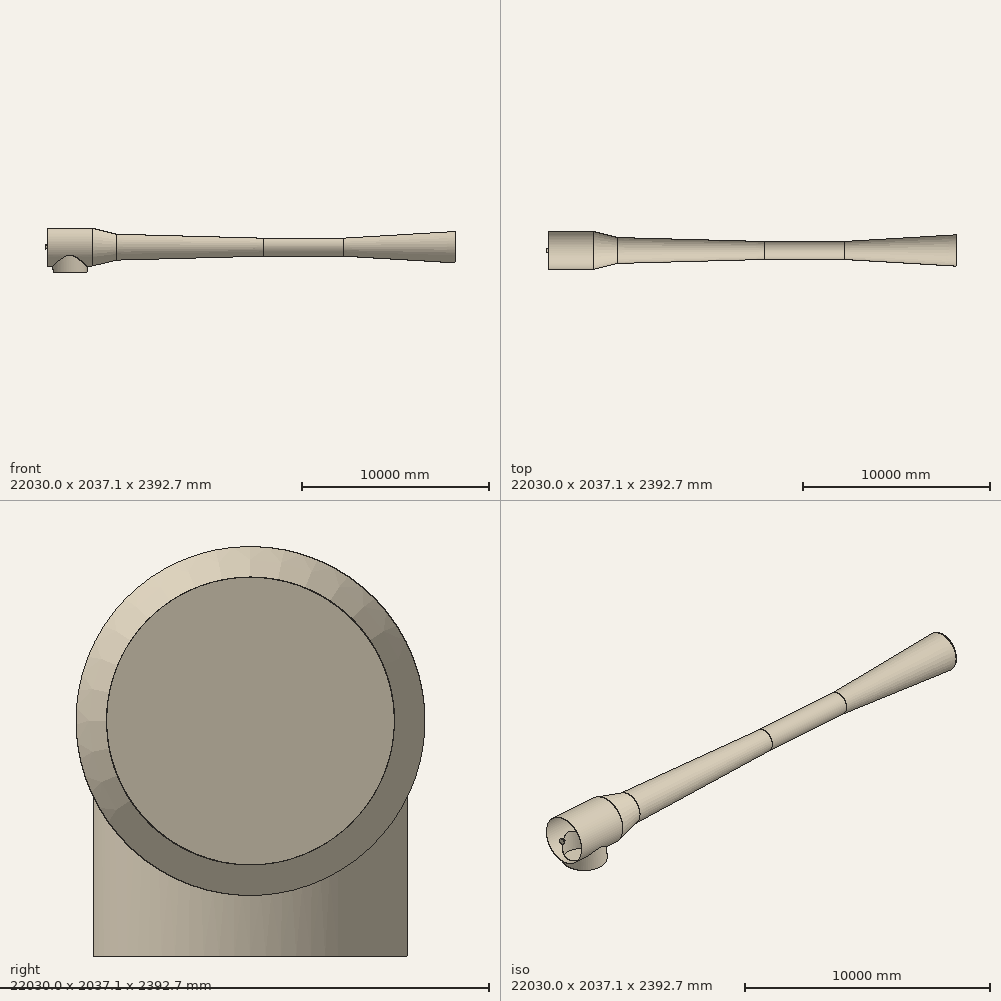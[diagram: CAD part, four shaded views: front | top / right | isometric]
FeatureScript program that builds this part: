
annotation { "Feature Type Name" : "Feature", "Feature Type Description" : "" }
export const myFeature = defineFeature(function(context is Context, id is Id, definition is map)
    precondition{}
    {
        {
            var Q0;
            Q0=qCreatedBy(makeId("Right.planeOp"),FACE);
            var sketch = newSketch(context, id + "F0", { "sketchPlane" : qUnion([Q0])});
            skCircle(sketch, "E0", {"center": v(0, 0) * mm, "radius": 1017.27 * mm});
            skSolve(sketch);
        }
        {
            var Q0;
            Q0 = qSketchRegion(id + "F0", true);
            extrude(context, id + "F1", {"entities" : qUnion([Q0]), "oppositeDirection" : true, "depth" : 2389.63 * mm});
        }
        {
            var Q0;
            Q0=makeQuery(id+"F1.opExtrude","CAP_FACE",FACE,{"disambiguationData":[OSD([sQuery(id+"F0.wireOp",EDGE,"E0")])],"isStart":true});
            shell(context, id + "F2", {"entities" : qUnion([Q0]), "thickness" : 2.54 * mm});
        }
        {
            var Q0;
            Q0=qCreatedBy(makeId("Top.planeOp"),FACE);
            var sketch = newSketch(context, id + "F3", { "sketchPlane" : qUnion([Q0])});
            skLineSegment(sketch, "E1", {"start": v(0, 0) * mm, "end": v(-2389.63, 0) * mm, "construction": true});
            skLineSegment(sketch, "E2", {"start": v(0, 0) * mm, "end": v(-1194.82, 0) * mm, "construction": true});
            skCircle(sketch, "E3", {"center": v(-1194.82, 0) * mm, "radius": 914.4 * mm});
            skCircle(sketch, "E4", {"center": v(-1194.82, 0) * mm, "radius": 915.67 * mm});
            skSolve(sketch);
        }
        {
            var Q0;
            Q0 = qSketchRegion(id + "F3", true);
            extrude(context, id + "F4", {"entities" : qUnion([Q0]), "oppositeDirection" : true, "depth" : 1371.6 * mm});
        }
        {
            var Q0;
            Q0=qCreatedBy(makeId("Right.planeOp"),FACE);
            var sketch = newSketch(context, id + "F5", { "sketchPlane" : qUnion([Q0])});
            skCircle(sketch, "E5", {"center": v(0, 0) * mm, "radius": 33.13 * mm});
            skSolve(sketch);
        }
        {
            var Q0;
            Q0 = qSketchRegion(id + "F5", true);
            extrude(context, id + "F6", {"entities" : qUnion([Q0]), "operationType" : NewBodyOperationType.REMOVE, "oppositeDirection" : true, "depth" : 2389.63 * mm});
        }
        {
            var Q0;
            Q0=qCreatedBy(makeId("Top.planeOp"),FACE);
            var sketch = newSketch(context, id + "F7", { "sketchPlane" : qUnion([Q0])});
            skLineSegment(sketch, "E6", {"start": v(0, 0) * mm, "end": v(-1194.82, 0) * mm});
            skCircle(sketch, "E7", {"center": v(-1194.82, 0) * mm, "radius": 914.4 * mm});
            skSolve(sketch);
        }
        {
            var Q0;
            Q0 = qSketchRegion(id + "F7", true);
            extrude(context, id + "F8", {"entities" : qUnion([Q0]), "operationType" : NewBodyOperationType.REMOVE, "oppositeDirection" : true, "depth" : 1018.54 * mm});
        }
        {
            var Q0;
            Q0=qCreatedBy(makeId("Front.planeOp"),FACE);
            var sketch = newSketch(context, id + "F9", { "sketchPlane" : qUnion([Q0])});
            skLineSegment(sketch, "E8", {"start": v(0, 0) * mm, "end": v(-2389.63, 0) * mm, "construction": true});
            skLineSegment(sketch, "E9", {"start": v(-2389.63, 33.13) * mm, "end": v(-2389.63, -33.13) * mm, "construction": true});
            skLineSegment(sketch, "E10", {"start": v(-2389.63, 33.13) * mm, "end": v(-1410.29, 241.3) * mm});
            skLineSegment(sketch, "E11", {"start": v(-2389.63, 33.13) * mm, "end": v(-2487.4, 101.59) * mm});
            skLineSegment(sketch, "E12", {"start": v(-2389.63, 33.13) * mm, "end": v(-1410.29, 33.13) * mm, "construction": true});
            skLineSegment(sketch, "E13", {"start": v(-2389.63, 58.53) * mm, "end": v(-2389.63, -58.53) * mm, "construction": true});
            skLineSegment(sketch, "E14", {"start": v(-2389.63, 58.53) * mm, "end": v(-1410.29, 266.7) * mm});
            skLineSegment(sketch, "E15", {"start": v(-2389.63, 58.53) * mm, "end": v(-2487.4, 126.99) * mm});
            skLineSegment(sketch, "E16", {"start": v(-2389.63, -33.13) * mm, "end": v(-2389.63, -58.53) * mm});
            skLineSegment(sketch, "E17", {"start": v(-2389.63, 33.13) * mm, "end": v(-2389.63, 58.53) * mm});
            skLineSegment(sketch, "E18", {"start": v(-1410.29, 266.7) * mm, "end": v(-1410.29, 241.3) * mm});
            skLineSegment(sketch, "E19", {"start": v(-2487.41, 33.13) * mm, "end": v(-2389.63, 33.13) * mm, "construction": true});
            skLineSegment(sketch, "E20", {"start": v(-2487.4, 101.59) * mm, "end": v(-2487.4, 126.99) * mm});
            skSolve(sketch);
        }
        {
            var Q0;
            Q0 = qSketchRegion(id + "F9", true);
            var Q1;
            Q1=sQuery(id+"F9.wireOp",EDGE,"E8");
            revolve(context, id + "F10", {"entities" : qUnion([Q0]), "axis" : qUnion([Q1]), "revolveType" : RevolveType.FULL});
        }
        {
            var Q0;
            Q0=makeQuery(id+"F10.opRevolve","SWEPT_FACE",FACE,{"disambiguationData":[OSD([sQuery(id+"F9.wireOp",EDGE,"E18")])]});
            var sketch = newSketch(context, id + "F11", { "sketchPlane" : qUnion([Q0])});
            skCircle(sketch, "E21", {"center": v(0, 0) * mm, "radius": 266.7 * mm});
            skSolve(sketch);
        }
        {
            var Q0;
            Q0 = qSketchRegion(id + "F11", true);
            extrude(context, id + "F12", {"entities" : qUnion([Q0]), "operationType" : NewBodyOperationType.ADD, "depth" : 2.54 * mm});
        }
        {
            var Q0;
            Q0=qCreatedBy(makeId("Front.planeOp"),FACE);
            var sketch = newSketch(context, id + "F13", { "sketchPlane" : qUnion([Q0])});
            skLineSegment(sketch, "E22", {"start": v(0, 0) * mm, "end": v(1319.48, 0) * mm, "construction": true});
            skLineSegment(sketch, "E23", {"start": v(0, 0) * mm, "end": v(0, 1016) * mm, "construction": true});
            skLineSegment(sketch, "E24", {"start": v(1319.48, 0) * mm, "end": v(1319.48, 693.42) * mm, "construction": true});
            skLineSegment(sketch, "E25", {"start": v(0, 1016) * mm, "end": v(1319.48, 693.42) * mm});
            skLineSegment(sketch, "E26", {"start": v(0, 1018.54) * mm, "end": v(1319.48, 695.96) * mm});
            skLineSegment(sketch, "E27", {"start": v(0, 1016) * mm, "end": v(0, 1018.54) * mm});
            skLineSegment(sketch, "E28", {"start": v(1319.48, 695.96) * mm, "end": v(1319.48, 693.42) * mm});
            skSolve(sketch);
        }
        {
            var Q0;
            Q0 = qSketchRegion(id + "F13", true);
            var Q1;
            Q1=sQuery(id+"F13.wireOp",EDGE,"E22");
            revolve(context, id + "F14", {"operationType" : NewBodyOperationType.ADD, "entities" : qUnion([Q0]), "axis" : qUnion([Q1]), "revolveType" : RevolveType.FULL});
        }
        {
            var Q0;
            Q0=qCreatedBy(makeId("Front.planeOp"),FACE);
            var sketch = newSketch(context, id + "F15", { "sketchPlane" : qUnion([Q0])});
            skLineSegment(sketch, "E29", {"start": v(0, 0) * mm, "end": v(1319.48, 0) * mm, "construction": true});
            skLineSegment(sketch, "E30", {"start": v(1319.48, 0) * mm, "end": v(1319.48, 693.42) * mm, "construction": true});
            skLineSegment(sketch, "E31", {"start": v(1319.48, 0) * mm, "end": v(9201.6, 0) * mm, "construction": true});
            skLineSegment(sketch, "E32", {"start": v(9201.6, 0) * mm, "end": v(9201.6, 481.01) * mm, "construction": true});
            skLineSegment(sketch, "E33", {"start": v(1319.48, 693.42) * mm, "end": v(9201.6, 481.01) * mm});
            skLineSegment(sketch, "E34", {"start": v(1319.48, 695.96) * mm, "end": v(9201.6, 483.55) * mm});
            skLineSegment(sketch, "E35", {"start": v(9201.6, 481.01) * mm, "end": v(9201.6, 483.55) * mm});
            skLineSegment(sketch, "E36", {"start": v(1319.48, 695.96) * mm, "end": v(1319.48, 693.42) * mm});
            skSolve(sketch);
        }
        {
            var Q0;
            Q0 = qSketchRegion(id + "F15", true);
            var Q1;
            Q1=sQuery(id+"F15.wireOp",EDGE,"E31");
            revolve(context, id + "F16", {"operationType" : NewBodyOperationType.ADD, "entities" : qUnion([Q0]), "axis" : qUnion([Q1]), "revolveType" : RevolveType.FULL});
        }
        {
            var Q0;
            Q0=makeQuery(id+"F16.opRevolve","SWEPT_FACE",FACE,{"disambiguationData":[OSD([sQuery(id+"F15.wireOp",EDGE,"E35")])]});
            var sketch = newSketch(context, id + "F17", { "sketchPlane" : qUnion([Q0])});
            skCircle(sketch, "E37", {"center": v(0, 0) * mm, "radius": 481.01 * mm});
            skCircle(sketch, "E38", {"center": v(0, 0) * mm, "radius": 482.28 * mm});
            skSolve(sketch);
        }
        {
            var Q0;
            Q0 = qSketchRegion(id + "F17", true);
            extrude(context, id + "F18", {"entities" : qUnion([Q0]), "operationType" : NewBodyOperationType.ADD, "depth" : 4302.12 * mm});
        }
        {
            var Q0;
            Q0=qCreatedBy(makeId("Front.planeOp"),FACE);
            var sketch = newSketch(context, id + "F19", { "sketchPlane" : qUnion([Q0])});
            skLineSegment(sketch, "E39", {"start": v(0, 0) * mm, "end": v(13503.73, 0) * mm, "construction": true});
            skLineSegment(sketch, "E40", {"start": v(13503.73, 0) * mm, "end": v(13503.73, 481.01) * mm, "construction": true});
            skLineSegment(sketch, "E41", {"start": v(13503.73, 0) * mm, "end": v(19491.78, 0) * mm, "construction": true});
            skLineSegment(sketch, "E42", {"start": v(19491.78, 0) * mm, "end": v(19491.78, 838.2) * mm, "construction": true});
            skLineSegment(sketch, "E43", {"start": v(13503.73, 481.01) * mm, "end": v(19491.78, 838.2) * mm});
            skLineSegment(sketch, "E44", {"start": v(13503.73, 481.01) * mm, "end": v(13503.73, 483.55) * mm});
            skLineSegment(sketch, "E45", {"start": v(13503.73, 483.55) * mm, "end": v(19491.78, 840.74) * mm});
            skLineSegment(sketch, "E46", {"start": v(19491.78, 840.74) * mm, "end": v(19491.78, 838.2) * mm});
            skSolve(sketch);
        }
        {
            var Q0;
            Q0 = qSketchRegion(id + "F19", true);
            var Q1;
            Q1=sQuery(id+"F19.wireOp",EDGE,"E41");
            revolve(context, id + "F20", {"operationType" : NewBodyOperationType.ADD, "entities" : qUnion([Q0]), "axis" : qUnion([Q1]), "revolveType" : RevolveType.FULL});
        }
        {
            var Q0;
            Q0=qCreatedBy(makeId("Right.planeOp"),FACE);
            var sketch = newSketch(context, id + "F21", { "sketchPlane" : qUnion([Q0])});
            skCircle(sketch, "E47", {"center": v(0, 0) * mm, "radius": 1016 * mm});
            skSolve(sketch);
        }
        {
            var Q0;
            Q0 = qSketchRegion(id + "F21", true);
            extrude(context, id + "F22", {"entities" : qUnion([Q0]), "operationType" : NewBodyOperationType.REMOVE, "oppositeDirection" : true, "depth" : 2389.63 * mm});
        }
        {
            var Q0;
            Q0=qCreatedBy(makeId("Top.planeOp"),FACE);
            var sketch = newSketch(context, id + "F23", { "sketchPlane" : qUnion([Q0])});
            skLineSegment(sketch, "E48", {"start": v(0, 0) * mm, "end": v(-1194.82, 0) * mm, "construction": true});
            skCircle(sketch, "E49", {"center": v(-1194.82, 0) * mm, "radius": 915.67 * mm});
            skSolve(sketch);
        }
        {
            var Q0;
            Q0=makeQuery(id+"F23.imprint","IMPRINT",FACE,{"disambiguationData":[TD([[makeQuery(id+"F23.imprint","IMPRINT",EDGE,{"derivedFrom":sQuery(id+"F23.wireOp",EDGE,"E49")}),1.0]])]});
            extrude(context, id + "F24", {"entities" : qUnion([Q0]), "operationType" : NewBodyOperationType.ADD, "oppositeDirection" : true, "depth" : 1374.14 * mm, "hasSecondDirection" : true, "secondDirectionOppositeDirection" : true, "secondDirectionDepth" : 1371.6 * mm});
        }
        {
            var Q0;
            Q0=makeQuery(id+"F10.opRevolve","SWEPT_FACE",FACE,{"disambiguationData":[OSD([sQuery(id+"F9.wireOp",EDGE,"E20")])]});
            var sketch = newSketch(context, id + "F25", { "sketchPlane" : qUnion([Q0])});
            skCircle(sketch, "E50", {"center": v(0, 0) * mm, "radius": 127 * mm});
            skSolve(sketch);
        }
        {
            var Q0;
            Q0 = qSketchRegion(id + "F25", true);
            extrude(context, id + "F26", {"entities" : qUnion([Q0]), "operationType" : NewBodyOperationType.ADD, "depth" : 25.4 * mm});
        }
        {
            var Q0;
            Q0=makeQuery(id+"F20.opRevolve","SWEPT_FACE",FACE,{"disambiguationData":[OSD([sQuery(id+"F19.wireOp",EDGE,"E46")])]});
            var sketch = newSketch(context, id + "F27", { "sketchPlane" : qUnion([Q0])});
            skCircle(sketch, "E51", {"center": v(0, 0) * mm, "radius": 839.47 * mm});
            skSolve(sketch);
        }
        {
            var Q0;
            Q0 = qSketchRegion(id + "F27", true);
            extrude(context, id + "F28", {"entities" : qUnion([Q0]), "operationType" : NewBodyOperationType.ADD, "depth" : 25.4 * mm});
        }
    });
